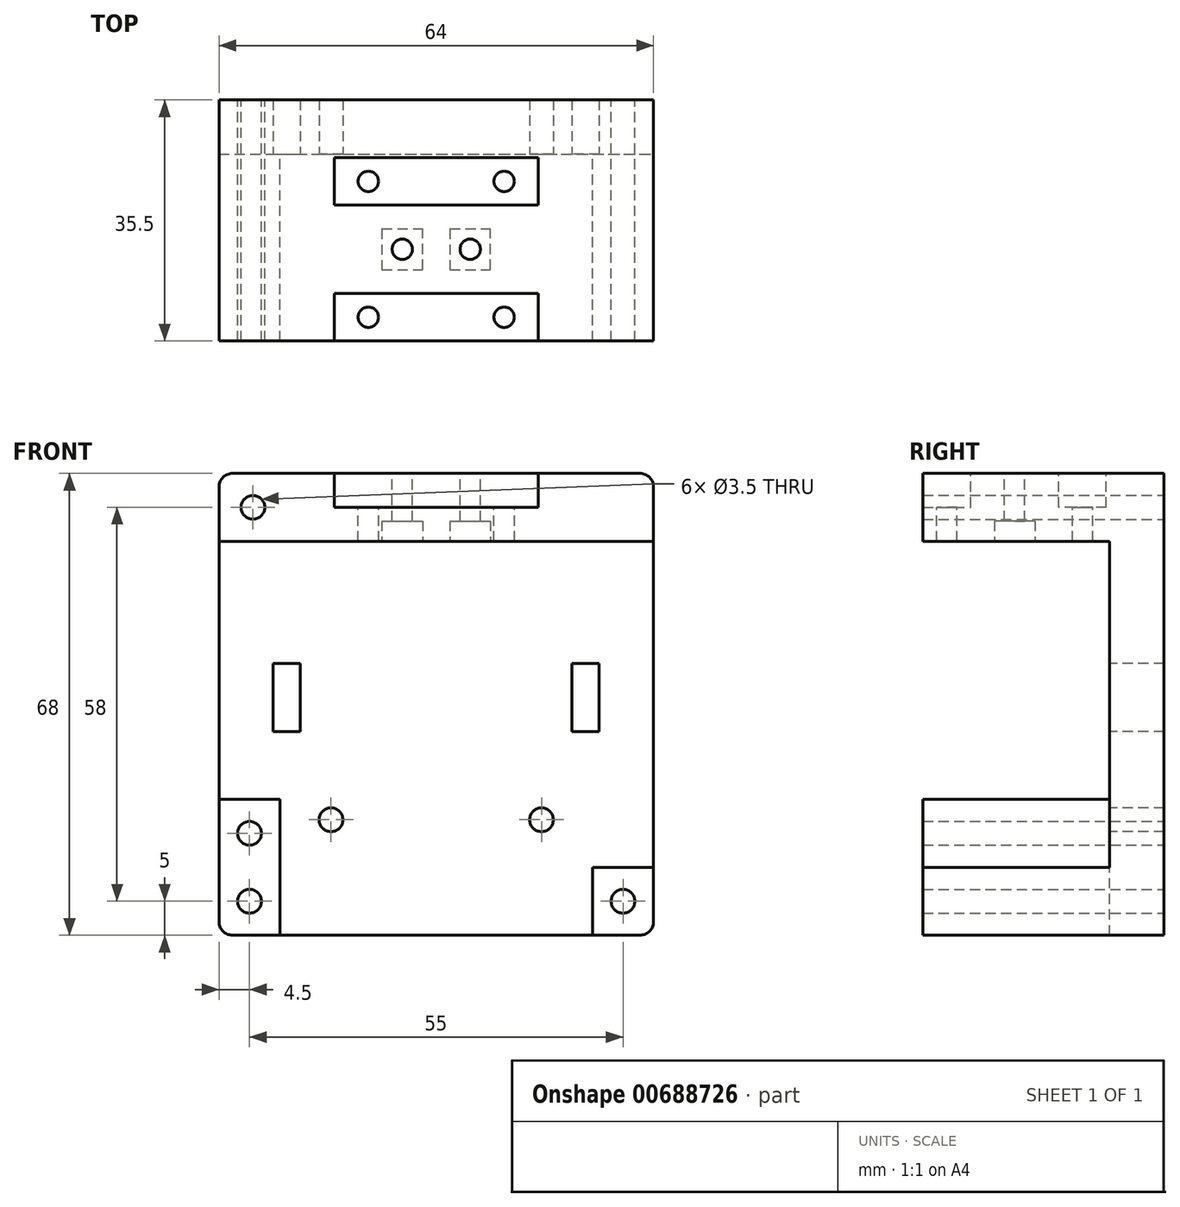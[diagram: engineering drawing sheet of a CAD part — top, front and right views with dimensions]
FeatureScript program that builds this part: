
annotation { "Feature Type Name" : "Feature", "Feature Type Description" : "" }
export const myFeature = defineFeature(function(context is Context, id is Id, definition is map)
    precondition{}
    {
        {
            var Q0;
            Q0=qCreatedBy(makeId("Front.planeOp"),FACE);
            var sketch = newSketch(context, id + "F0", { "sketchPlane" : qUnion([Q0])});
            skLineSegment(sketch, "E0.bottom", {"start": v(-32, 34) * mm, "end": v(32, 34) * mm});
            skLineSegment(sketch, "E0.top", {"start": v(-32, -34) * mm, "end": v(32, -34) * mm});
            skLineSegment(sketch, "E0.left", {"start": v(-32, 34) * mm, "end": v(-32, -34) * mm});
            skLineSegment(sketch, "E0.right", {"start": v(32, 34) * mm, "end": v(32, -34) * mm});
            skPoint(sketch, "E0.middle", {"position": v(0, 0) * mm});
            skSolve(sketch);
        }
        {
            var Q0;
            Q0=qSketchRegion(id+"F0",true);
            extrude(context, id + "F1", {"entities" : qUnion([Q0]), "depth" : 8 * mm, "offsetDistance" : 25 * mm});
        }
        {
            var Q0;
            Q0=makeQuery(id+"F1.opExtrude","CAP_FACE",FACE,{"disambiguationData":[OSD([sQuery(id+"F0.wireOp",EDGE,"E0.bottom"),sQuery(id+"F0.wireOp",EDGE,"E0.top"),sQuery(id+"F0.wireOp",EDGE,"E0.left"),sQuery(id+"F0.wireOp",EDGE,"E0.right")])],"isStart":false});
            var sketch = newSketch(context, id + "F2", { "sketchPlane" : qUnion([Q0])});
            skLineSegment(sketch, "E1.bottom", {"start": v(-32, 34) * mm, "end": v(32, 34) * mm});
            skLineSegment(sketch, "E1.top", {"start": v(-32, 24) * mm, "end": v(32, 24) * mm});
            skLineSegment(sketch, "E1.left", {"start": v(-32, 34) * mm, "end": v(-32, 24) * mm});
            skLineSegment(sketch, "E1.right", {"start": v(32, 34) * mm, "end": v(32, 24) * mm});
            skLineSegment(sketch, "E2", {"start": v(-32, 34) * mm, "end": v(-27, 34) * mm});
            skLineSegment(sketch, "E3", {"start": v(32, 34) * mm, "end": v(27, 34) * mm});
            skPoint(sketch, "E4.centerSnap0", {"position": v(-32, 29) * mm});
            skLineSegment(sketch, "E5.bottom", {"start": v(-32, -34) * mm, "end": v(-23, -34) * mm});
            skLineSegment(sketch, "E5.top", {"start": v(-32, -14) * mm, "end": v(-23, -14) * mm});
            skLineSegment(sketch, "E5.left", {"start": v(-32, -34) * mm, "end": v(-32, -14) * mm});
            skLineSegment(sketch, "E5.right", {"start": v(-23, -34) * mm, "end": v(-23, -14) * mm});
            skLineSegment(sketch, "E6.bottom", {"start": v(32, -34) * mm, "end": v(23, -34) * mm});
            skLineSegment(sketch, "E6.left", {"start": v(32, -34) * mm, "end": v(32, -24) * mm});
            skLineSegment(sketch, "E6.right", {"start": v(23, -34) * mm, "end": v(23, -24) * mm});
            skLineSegment(sketch, "E7", {"start": v(23, -24) * mm, "end": v(23, -24) * mm});
            skCircle(sketch, "E8", {"center": v(27.5, -29) * mm, "radius": 1.75 * mm});
            skPoint(sketch, "E8.centerSnap0", {"position": v(27.5, -34) * mm});
            skPoint(sketch, "E8.centerSnap1", {"position": v(23, -29) * mm});
            skCircle(sketch, "E9", {"center": v(-27.5, -19) * mm, "radius": 1.75 * mm});
            skPoint(sketch, "E9.centerSnap0", {"position": v(-27.5, -14) * mm});
            skCircle(sketch, "E10", {"center": v(-27.5, -29) * mm, "radius": 1.75 * mm});
            skPoint(sketch, "E10.centerSnap0", {"position": v(-27.5, -34) * mm});
            skCircle(sketch, "E11", {"center": v(27, 39) * mm, "radius": 1.75 * mm});
            skCircle(sketch, "E12", {"center": v(-27, 29) * mm, "radius": 1.75 * mm});
            skLineSegment(sketch, "E13", {"start": v(23, -24) * mm, "end": v(32, -24) * mm});
            skSolve(sketch);
        }
        {
            var Q0;
            {var subQ5=sQuery(id+"F2.wireOp",EDGE,"E1.bottom");Q0=makeQuery(id+"F2.imprint","IMPRINT",FACE,{"disambiguationData":[TD([[makeQuery(id+"F2.imprint","IMPRINT",EDGE,{"derivedFrom":subQ5}),-1.0]])]});}
            var Q1;
            {var subQ7=sQuery(id+"F2.wireOp",EDGE,"E1.left");Q1=makeQuery(id+"F2.imprint","IMPRINT",FACE,{"disambiguationData":[TD([[makeQuery(id+"F2.imprint","IMPRINT",EDGE,{"derivedFrom":subQ7}),1.0]])]});}
            var Q2;
            {var subQ4=sQuery(id+"F2.wireOp",EDGE,"E1.right");Q2=makeQuery(id+"F2.imprint","IMPRINT",FACE,{"disambiguationData":[TD([[makeQuery(id+"F2.imprint","IMPRINT",EDGE,{"derivedFrom":subQ4}),-1.0]])]});}
            var Q3;
            {var subQ0=sQuery(id+"F2.wireOp",EDGE,"Yd16WVRt-REVt-OFJK-DjKu-hKXUaHA9P329.left");Q3=makeQuery(id+"F2.imprint","IMPRINT",FACE,{"disambiguationData":[TD([[makeQuery(id+"F2.imprint","IMPRINT",EDGE,{"derivedFrom":subQ0}),1.0]])]});}
            var Q4;
            {var subQ5=sQuery(id+"F2.wireOp",EDGE,"Yd16WVRt-REVt-OFJK-DjKu-hKXUaHA9P329.right");Q4=makeQuery(id+"F2.imprint","IMPRINT",FACE,{"disambiguationData":[TD([[makeQuery(id+"F2.imprint","IMPRINT",EDGE,{"derivedFrom":subQ5}),1.0]])]});}
            var Q5;
            {var subQ5=sQuery(id+"F2.wireOp",EDGE,"CasWpeyr-yzLB-Kpzk-7YAV-Q1AeIs8uSEGq.right");Q5=makeQuery(id+"F2.imprint","IMPRINT",FACE,{"disambiguationData":[TD([[makeQuery(id+"F2.imprint","IMPRINT",EDGE,{"derivedFrom":subQ5}),-1.0]])]});}
            var Q6;
            {var subQ0=sQuery(id+"F2.wireOp",EDGE,"CasWpeyr-yzLB-Kpzk-7YAV-Q1AeIs8uSEGq.left");Q6=makeQuery(id+"F2.imprint","IMPRINT",FACE,{"disambiguationData":[TD([[makeQuery(id+"F2.imprint","IMPRINT",EDGE,{"derivedFrom":subQ0}),-1.0]])]});}
            var Q7;
            Q7=makeQuery(id+"F2.imprint","IMPRINT",FACE,{"disambiguationData":[TD([[makeQuery(id+"F2.imprint","IMPRINT",EDGE,{"derivedFrom":sQuery(id+"F2.wireOp",EDGE,"E5.bottom")}),1.0]])]});
            var Q8;
            Q8=makeQuery(id+"F2.imprint","IMPRINT",FACE,{"disambiguationData":[TD([[makeQuery(id+"F2.imprint","IMPRINT",EDGE,{"derivedFrom":sQuery(id+"F2.wireOp",EDGE,"E6.bottom")}),1.0]])]});
            extrude(context, id + "F3", {"entities" : qUnion([Q0, Q1, Q2, Q3, Q4, Q5, Q6, Q7, Q8]), "operationType" : NewBodyOperationType.ADD, "depth" : 27.5 * mm, "offsetDistance" : 25 * mm});
        }
        {
            var Q0;
            Q0=makeQuery(id+"F3.boolean.opBoolean","MERGE",FACE,{"derivedFrom":[makeQuery(id+"F1.opExtrude","SWEPT_FACE",FACE,{"disambiguationData":[OSD([sQuery(id+"F0.wireOp",EDGE,"E0.bottom")])]}),makeQuery(id+"F3.opExtrude","SWEPT_FACE",FACE,{"disambiguationData":[OSD([sQuery(id+"F2.wireOp",EDGE,"E1.bottom"),sQuery(id+"F2.wireOp",EDGE,"E2"),sQuery(id+"F2.wireOp",EDGE,"E3")])]})]});
            var sketch = newSketch(context, id + "F4", { "sketchPlane" : qUnion([Q0])});
            skLineSegment(sketch, "E14", {"start": v(0, -35.5) * mm, "end": v(-22, -35.5) * mm});
            skLineSegment(sketch, "E15", {"start": v(0, -35.5) * mm, "end": v(22, -35.5) * mm});
            skLineSegment(sketch, "E16", {"start": v(22, -35.5) * mm, "end": v(22, -8.5) * mm});
            skLineSegment(sketch, "E17", {"start": v(22, -8.5) * mm, "end": v(-22, -8.5) * mm});
            skLineSegment(sketch, "E18", {"start": v(-22, -8.5) * mm, "end": v(-22, -35.5) * mm});
            skLineSegment(sketch, "E19", {"start": v(-22, -22) * mm, "end": v(-22, -12) * mm});
            skLineSegment(sketch, "E20", {"start": v(-22, -22) * mm, "end": v(-22, -32) * mm});
            skLineSegment(sketch, "E21", {"start": v(-22, -12) * mm, "end": v(22, -12) * mm});
            skLineSegment(sketch, "E22", {"start": v(-22, -32) * mm, "end": v(22, -32) * mm});
            skLineSegment(sketch, "E23", {"start": v(0, -12) * mm, "end": v(-10, -12) * mm});
            skLineSegment(sketch, "E24", {"start": v(0, -12) * mm, "end": v(10, -12) * mm});
            skLineSegment(sketch, "E25", {"start": v(-10, -12) * mm, "end": v(-10, -32) * mm});
            skLineSegment(sketch, "E26", {"start": v(10, -12) * mm, "end": v(10, -32) * mm});
            skCircle(sketch, "E27", {"center": v(-10, -12) * mm, "radius": 1.5 * mm});
            skCircle(sketch, "E28", {"center": v(10, -12) * mm, "radius": 1.5 * mm});
            skCircle(sketch, "E29", {"center": v(10, -32) * mm, "radius": 1.5 * mm});
            skCircle(sketch, "E30", {"center": v(-10, -32) * mm, "radius": 1.5 * mm});
            skSolve(sketch);
        }
        {
            var Q0;
            {var subQ1=sQuery(id+"F4.wireOp",EDGE,"E21");var subQ3=sQuery(id+"F4.wireOp",EDGE,"E27");var subQ4=makeQuery(id+"F4.imprint","INTERSECT",VERTEX,{"derivedFrom":[subQ1,subQ3]});Q0=makeQuery(id+"F4.imprint","IMPRINT",FACE,{"disambiguationData":[TD([[makeQuery(id+"F4.imprint","IMPRINT",EDGE,{"disambiguationData":[TD([[subQ4,-1.0]])],"derivedFrom":subQ3}),1.0]])]});}
            var Q1;
            {var subQ1=sQuery(id+"F4.wireOp",EDGE,"E23");var subQ3=sQuery(id+"F4.wireOp",EDGE,"E27");var subQ4=makeQuery(id+"F4.imprint","INTERSECT",VERTEX,{"derivedFrom":[subQ1,subQ3]});Q1=makeQuery(id+"F4.imprint","IMPRINT",FACE,{"disambiguationData":[TD([[makeQuery(id+"F4.imprint","IMPRINT",EDGE,{"disambiguationData":[TD([[subQ4,1.0]])],"derivedFrom":subQ3}),1.0]])]});}
            var Q2;
            {var subQ1=sQuery(id+"F4.wireOp",EDGE,"E21");var subQ3=sQuery(id+"F4.wireOp",EDGE,"E27");var subQ4=makeQuery(id+"F4.imprint","INTERSECT",VERTEX,{"derivedFrom":[subQ1,subQ3]});Q2=makeQuery(id+"F4.imprint","IMPRINT",FACE,{"disambiguationData":[TD([[makeQuery(id+"F4.imprint","IMPRINT",EDGE,{"disambiguationData":[TD([[subQ4,1.0]])],"derivedFrom":subQ3}),1.0]])]});}
            var Q3;
            {var subQ0=sQuery(id+"F4.wireOp",EDGE,"E22");var subQ1=makeQuery(id+"F4.imprint","INTERSECT",VERTEX,{"derivedFrom":[subQ0,sQuery(id+"F4.wireOp",EDGE,"E25")]});Q3=makeQuery(id+"F4.imprint","IMPRINT",FACE,{"disambiguationData":[TD([[makeQuery(id+"F4.imprint","IMPRINT",EDGE,{"disambiguationData":[TD([[subQ1,1.0]])],"derivedFrom":subQ0}),-1.0]])]});}
            var Q4;
            {var subQ0=sQuery(id+"F4.wireOp",EDGE,"E25");var subQ1=sQuery(id+"F4.wireOp",EDGE,"E22");var subQ2=makeQuery(id+"F4.imprint","INTERSECT",VERTEX,{"derivedFrom":[subQ1,subQ0]});Q4=makeQuery(id+"F4.imprint","IMPRINT",FACE,{"disambiguationData":[TD([[makeQuery(id+"F4.imprint","IMPRINT",EDGE,{"disambiguationData":[TD([[subQ2,1.0]])],"derivedFrom":subQ1}),1.0]])]});}
            var Q5;
            {var subQ0=sQuery(id+"F4.wireOp",EDGE,"E25");var subQ1=sQuery(id+"F4.wireOp",EDGE,"E22");var subQ2=makeQuery(id+"F4.imprint","INTERSECT",VERTEX,{"derivedFrom":[subQ1,subQ0]});Q5=makeQuery(id+"F4.imprint","IMPRINT",FACE,{"disambiguationData":[TD([[makeQuery(id+"F4.imprint","IMPRINT",EDGE,{"disambiguationData":[TD([[subQ2,-1.0]])],"derivedFrom":subQ1}),1.0]])]});}
            var Q6;
            {var subQ0=sQuery(id+"F4.wireOp",EDGE,"E26");var subQ1=sQuery(id+"F4.wireOp",EDGE,"E22");var subQ2=makeQuery(id+"F4.imprint","INTERSECT",VERTEX,{"derivedFrom":[subQ1,subQ0]});Q6=makeQuery(id+"F4.imprint","IMPRINT",FACE,{"disambiguationData":[TD([[makeQuery(id+"F4.imprint","IMPRINT",EDGE,{"disambiguationData":[TD([[subQ2,1.0]])],"derivedFrom":subQ1}),1.0]])]});}
            var Q7;
            {var subQ0=sQuery(id+"F4.wireOp",EDGE,"E26");var subQ1=sQuery(id+"F4.wireOp",EDGE,"E22");var subQ2=makeQuery(id+"F4.imprint","INTERSECT",VERTEX,{"derivedFrom":[subQ1,subQ0]});Q7=makeQuery(id+"F4.imprint","IMPRINT",FACE,{"disambiguationData":[TD([[makeQuery(id+"F4.imprint","IMPRINT",EDGE,{"disambiguationData":[TD([[subQ2,-1.0]])],"derivedFrom":subQ1}),1.0]])]});}
            var Q8;
            {var subQ0=sQuery(id+"F4.wireOp",EDGE,"E22");var subQ1=makeQuery(id+"F4.imprint","INTERSECT",VERTEX,{"derivedFrom":[subQ0,sQuery(id+"F4.wireOp",EDGE,"E26")]});Q8=makeQuery(id+"F4.imprint","IMPRINT",FACE,{"disambiguationData":[TD([[makeQuery(id+"F4.imprint","IMPRINT",EDGE,{"disambiguationData":[TD([[subQ1,1.0]])],"derivedFrom":subQ0}),-1.0]])]});}
            var Q9;
            {var subQ1=sQuery(id+"F4.wireOp",EDGE,"E24");var subQ3=sQuery(id+"F4.wireOp",EDGE,"E28");var subQ4=makeQuery(id+"F4.imprint","INTERSECT",VERTEX,{"derivedFrom":[subQ1,subQ3]});Q9=makeQuery(id+"F4.imprint","IMPRINT",FACE,{"disambiguationData":[TD([[makeQuery(id+"F4.imprint","IMPRINT",EDGE,{"disambiguationData":[TD([[subQ4,-1.0]])],"derivedFrom":subQ3}),1.0]])]});}
            var Q10;
            {var subQ1=sQuery(id+"F4.wireOp",EDGE,"E21");var subQ3=sQuery(id+"F4.wireOp",EDGE,"E28");var subQ4=makeQuery(id+"F4.imprint","INTERSECT",VERTEX,{"derivedFrom":[subQ1,subQ3]});Q10=makeQuery(id+"F4.imprint","IMPRINT",FACE,{"disambiguationData":[TD([[makeQuery(id+"F4.imprint","IMPRINT",EDGE,{"disambiguationData":[TD([[subQ4,1.0]])],"derivedFrom":subQ3}),1.0]])]});}
            var Q11;
            {var subQ1=sQuery(id+"F4.wireOp",EDGE,"E21");var subQ3=sQuery(id+"F4.wireOp",EDGE,"E28");var subQ4=makeQuery(id+"F4.imprint","INTERSECT",VERTEX,{"derivedFrom":[subQ1,subQ3]});Q11=makeQuery(id+"F4.imprint","IMPRINT",FACE,{"disambiguationData":[TD([[makeQuery(id+"F4.imprint","IMPRINT",EDGE,{"disambiguationData":[TD([[subQ4,-1.0]])],"derivedFrom":subQ3}),1.0]])]});}
            extrude(context, id + "F5", {"entities" : qUnion([Q0, Q1, Q2, Q3, Q4, Q5, Q6, Q7, Q8, Q9, Q10, Q11]), "operationType" : NewBodyOperationType.REMOVE, "oppositeDirection" : true, "depth" : 25 * mm, "offsetDistance" : 25 * mm});
        }
        {
            var Q0;
            Q0=makeQuery(id+"F3.boolean.opBoolean","MERGE",FACE,{"derivedFrom":[makeQuery(id+"F1.opExtrude","SWEPT_FACE",FACE,{"disambiguationData":[OSD([sQuery(id+"F0.wireOp",EDGE,"E0.bottom")])]}),makeQuery(id+"F3.opExtrude","SWEPT_FACE",FACE,{"disambiguationData":[OSD([sQuery(id+"F2.wireOp",EDGE,"E1.bottom"),sQuery(id+"F2.wireOp",EDGE,"E2"),sQuery(id+"F2.wireOp",EDGE,"E3")])]})]});
            var sketch = newSketch(context, id + "F6", { "sketchPlane" : qUnion([Q0])});
            skLineSegment(sketch, "E31", {"start": v(0, -35.5) * mm, "end": v(-15, -35.5) * mm});
            skLineSegment(sketch, "E32", {"start": v(0, -35.5) * mm, "end": v(15, -35.5) * mm});
            skLineSegment(sketch, "E33", {"start": v(-15, -35.5) * mm, "end": v(-15, -28.5) * mm});
            skLineSegment(sketch, "E34", {"start": v(-15, -28.5) * mm, "end": v(15, -28.5) * mm});
            skLineSegment(sketch, "E35", {"start": v(15, -28.5) * mm, "end": v(15, -35.5) * mm});
            skLineSegment(sketch, "E36", {"start": v(-10, -12) * mm, "end": v(-15, -12) * mm});
            skLineSegment(sketch, "E37", {"start": v(-15, -12) * mm, "end": v(-15, -8.5) * mm});
            skLineSegment(sketch, "E38", {"start": v(-15, -8.5) * mm, "end": v(-15, -15.5) * mm});
            skLineSegment(sketch, "E39", {"start": v(10, -12) * mm, "end": v(15, -12) * mm});
            skLineSegment(sketch, "E40", {"start": v(15, -12) * mm, "end": v(15, -15.5) * mm});
            skLineSegment(sketch, "E41", {"start": v(15, -15.5) * mm, "end": v(15, -8.5) * mm});
            skLineSegment(sketch, "E42", {"start": v(15, -8.5) * mm, "end": v(-15, -8.5) * mm});
            skLineSegment(sketch, "E43", {"start": v(-15, -15.5) * mm, "end": v(15, -15.5) * mm});
            skSolve(sketch);
        }
        {
            var Q0;
            Q0=qSketchRegion(id+"F6",true);
            extrude(context, id + "F7", {"entities" : qUnion([Q0]), "operationType" : NewBodyOperationType.REMOVE, "oppositeDirection" : true, "depth" : 5 * mm, "offsetDistance" : 25 * mm});
        }
        {
            var Q0;
            Q0=makeQuery(id+"F3.boolean.opBoolean","MERGE",FACE,{"derivedFrom":[makeQuery(id+"F1.opExtrude","SWEPT_FACE",FACE,{"disambiguationData":[OSD([sQuery(id+"F0.wireOp",EDGE,"E0.bottom")])]}),makeQuery(id+"F3.opExtrude","SWEPT_FACE",FACE,{"disambiguationData":[OSD([sQuery(id+"F2.wireOp",EDGE,"E1.bottom"),sQuery(id+"F2.wireOp",EDGE,"E2"),sQuery(id+"F2.wireOp",EDGE,"E3")])]})]});
            var sketch = newSketch(context, id + "F8", { "sketchPlane" : qUnion([Q0])});
            skLineSegment(sketch, "E44", {"start": v(15, -15.5) * mm, "end": v(15, -28.5) * mm});
            skLineSegment(sketch, "E45", {"start": v(5, -22) * mm, "end": v(0, -22) * mm});
            skCircle(sketch, "E46", {"center": v(-5, -22) * mm, "radius": 1.5 * mm});
            skCircle(sketch, "E47", {"center": v(5, -22) * mm, "radius": 1.5 * mm});
            skLineSegment(sketch, "E48", {"start": v(0, -15.5) * mm, "end": v(0, -22) * mm});
            skLineSegment(sketch, "E49", {"start": v(0, -22) * mm, "end": v(-5, -22) * mm});
            skSolve(sketch);
        }
        {
            var Q0;
            Q0=qSketchRegion(id+"F8",true);
            extrude(context, id + "F9", {"entities" : qUnion([Q0]), "operationType" : NewBodyOperationType.REMOVE, "oppositeDirection" : true, "depth" : 25 * mm, "offsetDistance" : 25 * mm});
        }
        {
            var Q0;
            Q0=makeQuery(id+"F3.opExtrude","SWEPT_FACE",FACE,{"disambiguationData":[OSD([sQuery(id+"F2.wireOp",EDGE,"E1.top")])]});
            var sketch = newSketch(context, id + "F10", { "sketchPlane" : qUnion([Q0])});
            skLineSegment(sketch, "E50", {"start": v(5, 22) * mm, "end": v(8, 22) * mm});
            skLineSegment(sketch, "E51", {"start": v(8, 22) * mm, "end": v(-5, 22) * mm});
            skLineSegment(sketch, "E52", {"start": v(-5, 22) * mm, "end": v(-8, 22) * mm});
            skLineSegment(sketch, "E53", {"start": v(-8, 22) * mm, "end": v(-8, 25) * mm});
            skLineSegment(sketch, "E54", {"start": v(5, 22) * mm, "end": v(2, 22) * mm});
            skLineSegment(sketch, "E55", {"start": v(-5, 22) * mm, "end": v(-2, 22) * mm});
            skLineSegment(sketch, "E56", {"start": v(2, 22) * mm, "end": v(2, 25) * mm});
            skLineSegment(sketch, "E57", {"start": v(2, 25) * mm, "end": v(8, 25) * mm});
            skLineSegment(sketch, "E58", {"start": v(-8, 25) * mm, "end": v(-2, 25) * mm});
            skLineSegment(sketch, "E59", {"start": v(8, 25) * mm, "end": v(8, 22) * mm});
            skLineSegment(sketch, "E60", {"start": v(-8, 22) * mm, "end": v(-8, 19) * mm});
            skLineSegment(sketch, "E61", {"start": v(-8, 19) * mm, "end": v(-2, 19) * mm});
            skLineSegment(sketch, "E62", {"start": v(-2, 19) * mm, "end": v(-2, 22) * mm});
            skLineSegment(sketch, "E63", {"start": v(2, 22) * mm, "end": v(2, 19) * mm});
            skLineSegment(sketch, "E64", {"start": v(2, 19) * mm, "end": v(8, 19) * mm});
            skLineSegment(sketch, "E65", {"start": v(8, 19) * mm, "end": v(8, 22) * mm});
            skLineSegment(sketch, "E66", {"start": v(-2, 25) * mm, "end": v(-2, 22) * mm});
            skSolve(sketch);
        }
        {
            var Q0;
            Q0=qSketchRegion(id+"F10",true);
            extrude(context, id + "F11", {"entities" : qUnion([Q0]), "operationType" : NewBodyOperationType.REMOVE, "oppositeDirection" : true, "depth" : 3 * mm, "offsetDistance" : 25 * mm});
        }
        {
            var Q0;
            Q0=makeQuery(id+"F3.boolean.opBoolean","SPLIT",FACE,{"disambiguationData":[TD([makeQuery(id+"F3.opExtrude","SWEPT_FACE",FACE,{"disambiguationData":[OSD([sQuery(id+"F2.wireOp",EDGE,"E4")])]})])],"derivedFrom":makeQuery(id+"F1.opExtrude","CAP_FACE",FACE,{"disambiguationData":[OSD([sQuery(id+"F0.wireOp",EDGE,"E0.bottom"),sQuery(id+"F0.wireOp",EDGE,"E0.top"),sQuery(id+"F0.wireOp",EDGE,"E0.left"),sQuery(id+"F0.wireOp",EDGE,"E0.right")])],"isStart":false})});
            var Q1;
            Q1=makeQuery(id+"F3.boolean.opBoolean","SPLIT",FACE,{"disambiguationData":[TD([makeQuery(id+"F3.opExtrude","SWEPT_FACE",FACE,{"disambiguationData":[OSD([sQuery(id+"F2.wireOp",EDGE,"ZvZAWqEd-CA94-Rpaa-SU6f-6qopx4zODHrz")])]})])],"derivedFrom":makeQuery(id+"F1.opExtrude","CAP_FACE",FACE,{"disambiguationData":[OSD([sQuery(id+"F0.wireOp",EDGE,"E0.bottom"),sQuery(id+"F0.wireOp",EDGE,"E0.top"),sQuery(id+"F0.wireOp",EDGE,"E0.left"),sQuery(id+"F0.wireOp",EDGE,"E0.right")])],"isStart":false})});
            var Q2;
            Q2=makeQuery(id+"F3.boolean.opBoolean","SPLIT",FACE,{"disambiguationData":[TD([makeQuery(id+"F3.opExtrude","SWEPT_FACE",FACE,{"disambiguationData":[OSD([sQuery(id+"F2.wireOp",EDGE,"Sl0mf3Jw-zp51-E5IY-kPNq-jfKYS2Xht1Hv")])]})])],"derivedFrom":makeQuery(id+"F1.opExtrude","CAP_FACE",FACE,{"disambiguationData":[OSD([sQuery(id+"F0.wireOp",EDGE,"E0.bottom"),sQuery(id+"F0.wireOp",EDGE,"E0.top"),sQuery(id+"F0.wireOp",EDGE,"E0.left"),sQuery(id+"F0.wireOp",EDGE,"E0.right")])],"isStart":false})});
            var Q3;
            Q3=makeQuery(id+"F3.boolean.opBoolean","SPLIT",FACE,{"disambiguationData":[TD([makeQuery(id+"F3.opExtrude","SWEPT_FACE",FACE,{"disambiguationData":[OSD([sQuery(id+"F2.wireOp",EDGE,"ueuH1zhY-iWYn-hRMC-Si5H-fBq8uUvHrsYg")])]})])],"derivedFrom":makeQuery(id+"F1.opExtrude","CAP_FACE",FACE,{"disambiguationData":[OSD([sQuery(id+"F0.wireOp",EDGE,"E0.bottom"),sQuery(id+"F0.wireOp",EDGE,"E0.top"),sQuery(id+"F0.wireOp",EDGE,"E0.left"),sQuery(id+"F0.wireOp",EDGE,"E0.right")])],"isStart":false})});
            var Q4;
            Q4=makeQuery(id+"F3.boolean.opBoolean","SPLIT",FACE,{"disambiguationData":[TD([makeQuery(id+"F3.opExtrude","SWEPT_FACE",FACE,{"disambiguationData":[OSD([sQuery(id+"F2.wireOp",EDGE,"FCoazugY-MPN5-JA2A-m2Li-t61wZpry6vJ0")])]})])],"derivedFrom":makeQuery(id+"F1.opExtrude","CAP_FACE",FACE,{"disambiguationData":[OSD([sQuery(id+"F0.wireOp",EDGE,"E0.bottom"),sQuery(id+"F0.wireOp",EDGE,"E0.top"),sQuery(id+"F0.wireOp",EDGE,"E0.left"),sQuery(id+"F0.wireOp",EDGE,"E0.right")])],"isStart":false})});
            var Q5;
            Q5=makeQuery(id+"F3.boolean.opBoolean","SPLIT",FACE,{"disambiguationData":[TD([makeQuery(id+"F3.opExtrude","SWEPT_FACE",FACE,{"disambiguationData":[OSD([sQuery(id+"F2.wireOp",EDGE,"NHk6pnkp-Mi0x-RU7y-kxS4-8469h8htnUJA")])]})])],"derivedFrom":makeQuery(id+"F1.opExtrude","CAP_FACE",FACE,{"disambiguationData":[OSD([sQuery(id+"F0.wireOp",EDGE,"E0.bottom"),sQuery(id+"F0.wireOp",EDGE,"E0.top"),sQuery(id+"F0.wireOp",EDGE,"E0.left"),sQuery(id+"F0.wireOp",EDGE,"E0.right")])],"isStart":false})});
            var Q6;
            Q6=makeQuery(id+"F3.boolean.opBoolean","SPLIT",FACE,{"disambiguationData":[TD([makeQuery(id+"F3.opExtrude","SWEPT_FACE",FACE,{"disambiguationData":[OSD([sQuery(id+"F2.wireOp",EDGE,"E8")])]})])],"derivedFrom":makeQuery(id+"F1.opExtrude","CAP_FACE",FACE,{"disambiguationData":[OSD([sQuery(id+"F0.wireOp",EDGE,"E0.bottom"),sQuery(id+"F0.wireOp",EDGE,"E0.top"),sQuery(id+"F0.wireOp",EDGE,"E0.left"),sQuery(id+"F0.wireOp",EDGE,"E0.right")])],"isStart":false})});
            var Q7;
            Q7=makeQuery(id+"F3.boolean.opBoolean","SPLIT",FACE,{"disambiguationData":[TD([makeQuery(id+"F3.opExtrude","SWEPT_FACE",FACE,{"disambiguationData":[OSD([sQuery(id+"F2.wireOp",EDGE,"K1OWNs7A-DZ5T-bWwp-Ejm7-NK7mQgMPgbh3")])]})])],"derivedFrom":makeQuery(id+"F1.opExtrude","CAP_FACE",FACE,{"disambiguationData":[OSD([sQuery(id+"F0.wireOp",EDGE,"E0.bottom"),sQuery(id+"F0.wireOp",EDGE,"E0.top"),sQuery(id+"F0.wireOp",EDGE,"E0.left"),sQuery(id+"F0.wireOp",EDGE,"E0.right")])],"isStart":false})});
            var Q8;
            Q8=makeQuery(id+"F3.boolean.opBoolean","SPLIT",FACE,{"disambiguationData":[TD([makeQuery(id+"F3.opExtrude","SWEPT_FACE",FACE,{"disambiguationData":[OSD([sQuery(id+"F2.wireOp",EDGE,"E9")])]})])],"derivedFrom":makeQuery(id+"F1.opExtrude","CAP_FACE",FACE,{"disambiguationData":[OSD([sQuery(id+"F0.wireOp",EDGE,"E0.bottom"),sQuery(id+"F0.wireOp",EDGE,"E0.top"),sQuery(id+"F0.wireOp",EDGE,"E0.left"),sQuery(id+"F0.wireOp",EDGE,"E0.right")])],"isStart":false})});
            var Q9;
            Q9=makeQuery(id+"F3.boolean.opBoolean","SPLIT",FACE,{"disambiguationData":[TD([makeQuery(id+"F3.opExtrude","SWEPT_FACE",FACE,{"disambiguationData":[OSD([sQuery(id+"F2.wireOp",EDGE,"E10")])]})])],"derivedFrom":makeQuery(id+"F1.opExtrude","CAP_FACE",FACE,{"disambiguationData":[OSD([sQuery(id+"F0.wireOp",EDGE,"E0.bottom"),sQuery(id+"F0.wireOp",EDGE,"E0.top"),sQuery(id+"F0.wireOp",EDGE,"E0.left"),sQuery(id+"F0.wireOp",EDGE,"E0.right")])],"isStart":false})});
            var Q10;
            Q10=makeQuery(id+"F3.boolean.opBoolean","SPLIT",FACE,{"disambiguationData":[TD([makeQuery(id+"F3.opExtrude","SWEPT_FACE",FACE,{"disambiguationData":[OSD([sQuery(id+"F2.wireOp",EDGE,"E11")])]})])],"derivedFrom":makeQuery(id+"F1.opExtrude","CAP_FACE",FACE,{"disambiguationData":[OSD([sQuery(id+"F0.wireOp",EDGE,"E0.bottom"),sQuery(id+"F0.wireOp",EDGE,"E0.top"),sQuery(id+"F0.wireOp",EDGE,"E0.left"),sQuery(id+"F0.wireOp",EDGE,"E0.right")])],"isStart":false})});
            var Q11;
            Q11=makeQuery(id+"F3.boolean.opBoolean","SPLIT",FACE,{"disambiguationData":[TD([makeQuery(id+"F3.opExtrude","SWEPT_FACE",FACE,{"disambiguationData":[OSD([sQuery(id+"F2.wireOp",EDGE,"E12")])]})])],"derivedFrom":makeQuery(id+"F1.opExtrude","CAP_FACE",FACE,{"disambiguationData":[OSD([sQuery(id+"F0.wireOp",EDGE,"E0.bottom"),sQuery(id+"F0.wireOp",EDGE,"E0.top"),sQuery(id+"F0.wireOp",EDGE,"E0.left"),sQuery(id+"F0.wireOp",EDGE,"E0.right")])],"isStart":false})});
            extrude(context, id + "F12", {"entities" : qUnion([Q0, Q1, Q2, Q3, Q4, Q5, Q6, Q7, Q8, Q9, Q10, Q11]), "operationType" : NewBodyOperationType.REMOVE, "oppositeDirection" : true, "depth" : 25 * mm, "offsetDistance" : 25 * mm});
        }
        {
            var Q0;
            {var subQ0=sQuery(id+"F0.wireOp",EDGE,"E0.top");var subQ1=sQuery(id+"F0.wireOp",EDGE,"E0.right");var subQ2=sQuery(id+"F0.wireOp",EDGE,"E0.left");Q0=makeQuery(id+"F3.boolean.opBoolean","SPLIT",FACE,{"disambiguationData":[TD([makeQuery(id+"F1.opExtrude","SWEPT_FACE",FACE,{"disambiguationData":[OSD([subQ0])]})])],"derivedFrom":makeQuery(id+"F1.opExtrude","CAP_FACE",FACE,{"disambiguationData":[OSD([sQuery(id+"F0.wireOp",EDGE,"E0.bottom"),subQ0,subQ2,subQ1])],"isStart":false})});}
            var sketch = newSketch(context, id + "F13", { "sketchPlane" : qUnion([Q0])});
            skLineSegment(sketch, "E67", {"start": v(0, 24) * mm, "end": v(0, -11) * mm});
            skLineSegment(sketch, "E68", {"start": v(32, -11) * mm, "end": v(-32, -11) * mm});
            skLineSegment(sketch, "E69", {"start": v(0, -11) * mm, "end": v(-21.5, -11) * mm});
            skLineSegment(sketch, "E70", {"start": v(-21.5, -11) * mm, "end": v(21.5, -11) * mm});
            skLineSegment(sketch, "E71", {"start": v(21.5, -11) * mm, "end": v(21.5, -54) * mm});
            skLineSegment(sketch, "E72", {"start": v(21.5, -54) * mm, "end": v(-21.5, -54) * mm});
            skLineSegment(sketch, "E73", {"start": v(-21.5, -54) * mm, "end": v(-21.5, -11) * mm});
            skLineSegment(sketch, "E74.bottom", {"start": v(-15.5, -17) * mm, "end": v(15.5, -17) * mm});
            skLineSegment(sketch, "E74.top", {"start": v(-15.5, -48) * mm, "end": v(15.5, -48) * mm});
            skLineSegment(sketch, "E74.left", {"start": v(-15.5, -17) * mm, "end": v(-15.5, -48) * mm});
            skLineSegment(sketch, "E74.right", {"start": v(15.5, -17) * mm, "end": v(15.5, -48) * mm});
            skPoint(sketch, "E74.middle", {"position": v(0, -32.5) * mm});
            skPoint(sketch, "E74.middle.positionSnap0", {"position": v(0, -54) * mm});
            skPoint(sketch, "E74.middle.positionSnap1", {"position": v(-21.5, -32.5) * mm});
            skPoint(sketch, "E74.centerSnap0", {"position": v(0, -54) * mm});
            skPoint(sketch, "E74.centerSnap1", {"position": v(-21.5, -32.5) * mm});
            skCircle(sketch, "E75", {"center": v(-15.5, -17) * mm, "radius": 1.75 * mm});
            skCircle(sketch, "E76", {"center": v(15.5, -17) * mm, "radius": 1.75 * mm});
            skCircle(sketch, "E77", {"center": v(-15.5, -48) * mm, "radius": 1.75 * mm});
            skCircle(sketch, "E78", {"center": v(15.5, -48) * mm, "radius": 1.75 * mm});
            skSolve(sketch);
        }
        {
            var Q0;
            {var subQ0=sQuery(id+"F13.wireOp",EDGE,"E74.left");var subQ1=sQuery(id+"F13.wireOp",EDGE,"E74.bottom");var subQ2=makeQuery(id+"F13.imprint","INTERSECT",VERTEX,{"derivedFrom":[subQ1,subQ0]});Q0=makeQuery(id+"F13.imprint","IMPRINT",FACE,{"disambiguationData":[TD([[makeQuery(id+"F13.imprint","IMPRINT",EDGE,{"disambiguationData":[TD([[subQ2,-1.0]])],"derivedFrom":subQ1}),1.0]])]});}
            var Q1;
            {var subQ0=sQuery(id+"F13.wireOp",EDGE,"E74.left");var subQ1=sQuery(id+"F13.wireOp",EDGE,"E74.bottom");var subQ2=makeQuery(id+"F13.imprint","INTERSECT",VERTEX,{"derivedFrom":[subQ1,subQ0]});Q1=makeQuery(id+"F13.imprint","IMPRINT",FACE,{"disambiguationData":[TD([[makeQuery(id+"F13.imprint","IMPRINT",EDGE,{"disambiguationData":[TD([[subQ2,-1.0]])],"derivedFrom":subQ1}),-1.0]])]});}
            var Q2;
            {var subQ0=sQuery(id+"F13.wireOp",EDGE,"E74.right");var subQ1=sQuery(id+"F13.wireOp",EDGE,"E74.bottom");var subQ2=makeQuery(id+"F13.imprint","INTERSECT",VERTEX,{"derivedFrom":[subQ1,subQ0]});Q2=makeQuery(id+"F13.imprint","IMPRINT",FACE,{"disambiguationData":[TD([[makeQuery(id+"F13.imprint","IMPRINT",EDGE,{"disambiguationData":[TD([[subQ2,1.0]])],"derivedFrom":subQ1}),-1.0]])]});}
            var Q3;
            {var subQ0=sQuery(id+"F13.wireOp",EDGE,"E74.right");var subQ1=sQuery(id+"F13.wireOp",EDGE,"E74.bottom");var subQ2=makeQuery(id+"F13.imprint","INTERSECT",VERTEX,{"derivedFrom":[subQ1,subQ0]});Q3=makeQuery(id+"F13.imprint","IMPRINT",FACE,{"disambiguationData":[TD([[makeQuery(id+"F13.imprint","IMPRINT",EDGE,{"disambiguationData":[TD([[subQ2,1.0]])],"derivedFrom":subQ1}),1.0]])]});}
            var Q4;
            {var subQ0=sQuery(id+"F13.wireOp",EDGE,"E74.right");var subQ1=sQuery(id+"F13.wireOp",EDGE,"E74.top");var subQ2=makeQuery(id+"F13.imprint","INTERSECT",VERTEX,{"derivedFrom":[subQ1,subQ0]});Q4=makeQuery(id+"F13.imprint","IMPRINT",FACE,{"disambiguationData":[TD([[makeQuery(id+"F13.imprint","IMPRINT",EDGE,{"disambiguationData":[TD([[subQ2,1.0]])],"derivedFrom":subQ1}),1.0]])]});}
            var Q5;
            {var subQ0=sQuery(id+"F13.wireOp",EDGE,"E74.right");var subQ1=sQuery(id+"F13.wireOp",EDGE,"E74.top");var subQ2=makeQuery(id+"F13.imprint","INTERSECT",VERTEX,{"derivedFrom":[subQ1,subQ0]});Q5=makeQuery(id+"F13.imprint","IMPRINT",FACE,{"disambiguationData":[TD([[makeQuery(id+"F13.imprint","IMPRINT",EDGE,{"disambiguationData":[TD([[subQ2,1.0]])],"derivedFrom":subQ1}),-1.0]])]});}
            var Q6;
            {var subQ0=sQuery(id+"F13.wireOp",EDGE,"E74.left");var subQ1=sQuery(id+"F13.wireOp",EDGE,"E74.top");var subQ2=makeQuery(id+"F13.imprint","INTERSECT",VERTEX,{"derivedFrom":[subQ1,subQ0]});Q6=makeQuery(id+"F13.imprint","IMPRINT",FACE,{"disambiguationData":[TD([[makeQuery(id+"F13.imprint","IMPRINT",EDGE,{"disambiguationData":[TD([[subQ2,-1.0]])],"derivedFrom":subQ1}),1.0]])]});}
            var Q7;
            {var subQ0=sQuery(id+"F13.wireOp",EDGE,"E74.left");var subQ1=sQuery(id+"F13.wireOp",EDGE,"E74.top");var subQ2=makeQuery(id+"F13.imprint","INTERSECT",VERTEX,{"derivedFrom":[subQ1,subQ0]});Q7=makeQuery(id+"F13.imprint","IMPRINT",FACE,{"disambiguationData":[TD([[makeQuery(id+"F13.imprint","IMPRINT",EDGE,{"disambiguationData":[TD([[subQ2,-1.0]])],"derivedFrom":subQ1}),-1.0]])]});}
            extrude(context, id + "F14", {"entities" : qUnion([Q0, Q1, Q2, Q3, Q4, Q5, Q6, Q7]), "operationType" : NewBodyOperationType.REMOVE, "oppositeDirection" : true, "depth" : 25 * mm, "offsetDistance" : 25 * mm});
        }
        {
            var Q0;
            {var subQ0=sQuery(id+"F0.wireOp",EDGE,"E0.top");var subQ1=sQuery(id+"F0.wireOp",EDGE,"E0.right");var subQ2=sQuery(id+"F0.wireOp",EDGE,"E0.left");Q0=makeQuery(id+"F3.boolean.opBoolean","SPLIT",FACE,{"disambiguationData":[TD([makeQuery(id+"F1.opExtrude","SWEPT_FACE",FACE,{"disambiguationData":[OSD([subQ0])]})])],"derivedFrom":makeQuery(id+"F1.opExtrude","CAP_FACE",FACE,{"disambiguationData":[OSD([sQuery(id+"F0.wireOp",EDGE,"E0.bottom"),subQ0,subQ2,subQ1])],"isStart":false})});}
            var sketch = newSketch(context, id + "F15", { "sketchPlane" : qUnion([Q0])});
            skLineSegment(sketch, "E79", {"start": v(-24, 24) * mm, "end": v(-24, 6) * mm});
            skLineSegment(sketch, "E80.bottom", {"start": v(-24, 6) * mm, "end": v(-20, 6) * mm});
            skLineSegment(sketch, "E80.top", {"start": v(-24, -4) * mm, "end": v(-20, -4) * mm});
            skLineSegment(sketch, "E80.left", {"start": v(-24, 6) * mm, "end": v(-24, -4) * mm});
            skLineSegment(sketch, "E80.right", {"start": v(-20, 6) * mm, "end": v(-20, -4) * mm});
            skLineSegment(sketch, "E81", {"start": v(24, 24) * mm, "end": v(24, 6) * mm});
            skLineSegment(sketch, "E82.bottom", {"start": v(24, 6) * mm, "end": v(20, 6) * mm});
            skLineSegment(sketch, "E82.top", {"start": v(24, -4) * mm, "end": v(20, -4) * mm});
            skLineSegment(sketch, "E82.left", {"start": v(24, 6) * mm, "end": v(24, -4) * mm});
            skLineSegment(sketch, "E82.right", {"start": v(20, 6) * mm, "end": v(20, -4) * mm});
            skLineSegment(sketch, "E83", {"start": v(-24, 27.13) * mm, "end": v(-32, 27.13) * mm});
            skLineSegment(sketch, "E84", {"start": v(24, 15) * mm, "end": v(32, 15) * mm});
            skSolve(sketch);
        }
        {
            var Q0;
            Q0=qSketchRegion(id+"F15",true);
            extrude(context, id + "F16", {"entities" : qUnion([Q0]), "operationType" : NewBodyOperationType.REMOVE, "oppositeDirection" : true, "depth" : 25 * mm, "offsetDistance" : 25 * mm});
        }
        {
            var Q0;
            Q0=makeQuery(id+"F3.boolean.opBoolean","MERGE",EDGE,{"derivedFrom":[makeQuery(id+"F1.opExtrude","SWEPT_EDGE",EDGE,{"disambiguationData":[OSD([sQuery(id+"F0.wireOp",EDGE,"E0.top"),sQuery(id+"F0.wireOp",EDGE,"E0.right")])]}),makeQuery(id+"F3.opExtrude","SWEPT_EDGE",EDGE,{"disambiguationData":[OSD([sQuery(id+"F2.wireOp",EDGE,"E6.bottom"),sQuery(id+"F2.wireOp",EDGE,"E6.left")])]})]});
            var Q1;
            Q1=makeQuery(id+"F3.boolean.opBoolean","MERGE",EDGE,{"derivedFrom":[makeQuery(id+"F1.opExtrude","SWEPT_EDGE",EDGE,{"disambiguationData":[OSD([sQuery(id+"F0.wireOp",EDGE,"E0.bottom"),sQuery(id+"F0.wireOp",EDGE,"E0.right")])]}),makeQuery(id+"F3.opExtrude","SWEPT_EDGE",EDGE,{"disambiguationData":[OSD([sQuery(id+"F2.wireOp",EDGE,"E1.right"),sQuery(id+"F2.wireOp",EDGE,"E3")])]})]});
            var Q2;
            Q2=makeQuery(id+"F3.boolean.opBoolean","MERGE",EDGE,{"derivedFrom":[makeQuery(id+"F1.opExtrude","SWEPT_EDGE",EDGE,{"disambiguationData":[OSD([sQuery(id+"F0.wireOp",EDGE,"E0.top"),sQuery(id+"F0.wireOp",EDGE,"E0.left")])]}),makeQuery(id+"F3.opExtrude","SWEPT_EDGE",EDGE,{"disambiguationData":[OSD([sQuery(id+"F2.wireOp",EDGE,"E5.bottom"),sQuery(id+"F2.wireOp",EDGE,"E5.left")])]})]});
            var Q3;
            Q3=makeQuery(id+"F3.boolean.opBoolean","MERGE",EDGE,{"derivedFrom":[makeQuery(id+"F1.opExtrude","SWEPT_EDGE",EDGE,{"disambiguationData":[OSD([sQuery(id+"F0.wireOp",EDGE,"E0.bottom"),sQuery(id+"F0.wireOp",EDGE,"E0.left")])]}),makeQuery(id+"F3.opExtrude","SWEPT_EDGE",EDGE,{"disambiguationData":[OSD([sQuery(id+"F2.wireOp",EDGE,"E1.left"),sQuery(id+"F2.wireOp",EDGE,"E2")])]})]});
            fillet(context, id + "F17", {"entities" : qUnion([Q0, Q1, Q2, Q3]), "radius" : 2 * mm, "tangentPropagation" : true, "allowEdgeOverflow" : false});
        }
    });
